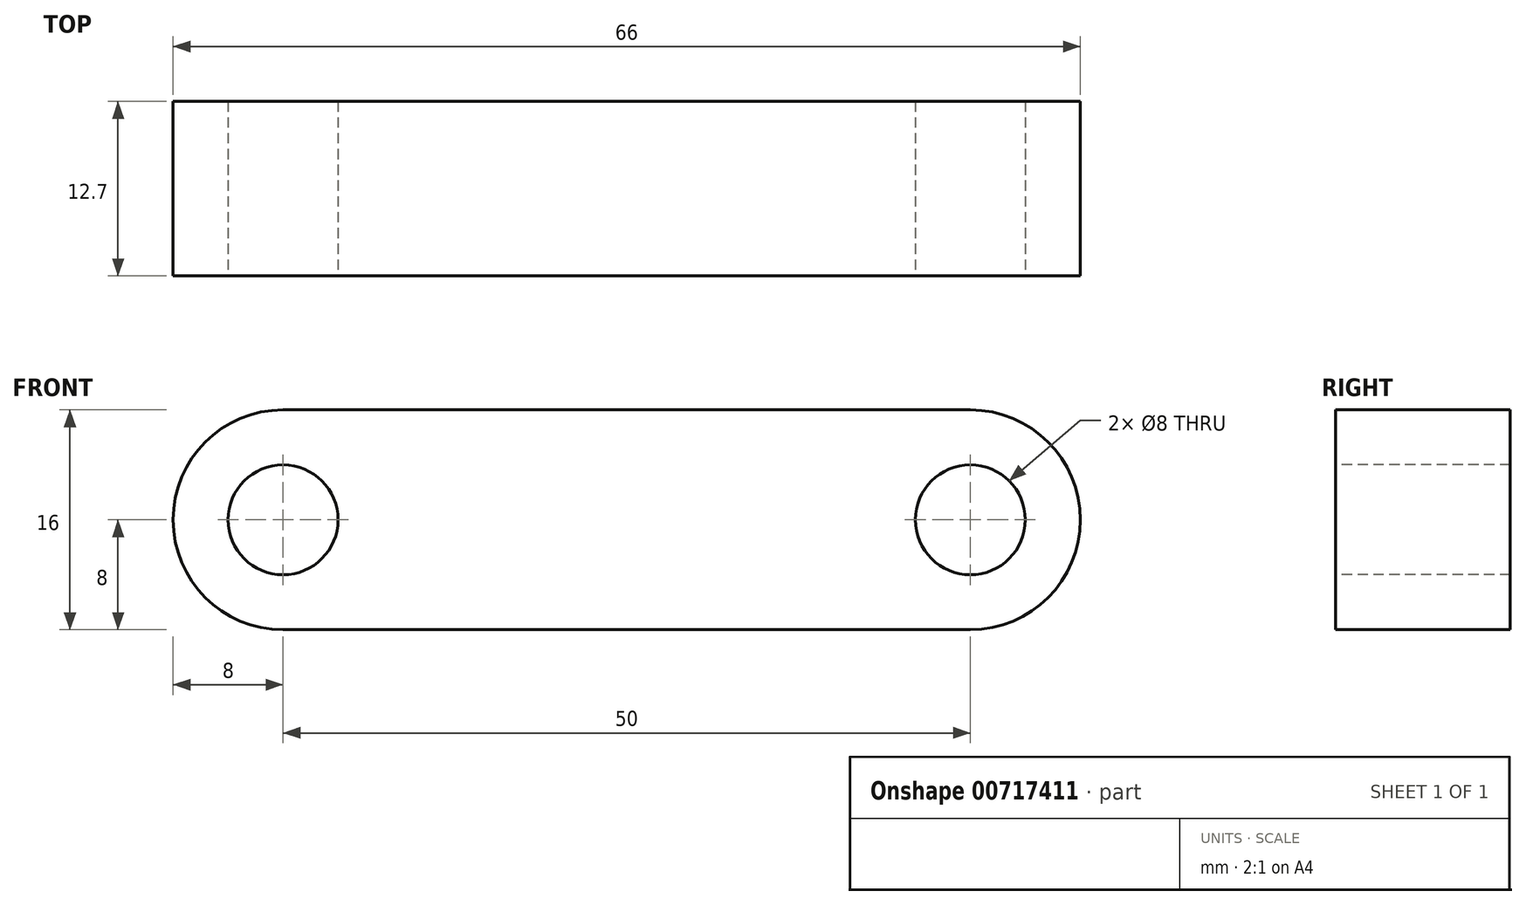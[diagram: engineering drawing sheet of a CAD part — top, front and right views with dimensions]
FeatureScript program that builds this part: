
annotation { "Feature Type Name" : "Feature", "Feature Type Description" : "" }
export const myFeature = defineFeature(function(context is Context, id is Id, definition is map)
    precondition{}
    {
        {
            var Q0;
            Q0=qCreatedBy(makeId("Front.planeOp"),FACE);
            var sketch = newSketch(context, id + "F0", { "sketchPlane" : qUnion([Q0])});
            skCircle(sketch, "E0", {"center": v(0, 0) * mm, "radius": 8 * mm});
            skCircle(sketch, "E1", {"center": v(-50, 0) * mm, "radius": 8 * mm});
            skLineSegment(sketch, "E2", {"start": v(-50, 8) * mm, "end": v(0, 8) * mm});
            skLineSegment(sketch, "E3", {"start": v(0, -8) * mm, "end": v(-50, -8) * mm});
            skSolve(sketch);
        }
        {
            var Q0;
            {var subQ0=sQuery(id+"F0.wireOp",EDGE,"E2");Q0=makeQuery(id+"F0.imprint","IMPRINT",FACE,{"disambiguationData":[TD([[makeQuery(id+"F0.imprint","IMPRINT",EDGE,{"derivedFrom":subQ0}),-1.0]])]});}
            var Q1;
            {var subQ0=sQuery(id+"F0.wireOp",EDGE,"E1");var subQ1=makeQuery(id+"F0.imprint","INTERSECT",VERTEX,{"derivedFrom":[subQ0,sQuery(id+"F0.wireOp",EDGE,"E2")]});Q1=makeQuery(id+"F0.imprint","IMPRINT",FACE,{"disambiguationData":[TD([[makeQuery(id+"F0.imprint","IMPRINT",EDGE,{"disambiguationData":[TD([[subQ1,-1.0]])],"derivedFrom":subQ0}),1.0]])]});}
            var Q2;
            {var subQ0=sQuery(id+"F0.wireOp",EDGE,"E0");var subQ1=makeQuery(id+"F0.imprint","INTERSECT",VERTEX,{"derivedFrom":[subQ0,sQuery(id+"F0.wireOp",EDGE,"E2")]});Q2=makeQuery(id+"F0.imprint","IMPRINT",FACE,{"disambiguationData":[TD([[makeQuery(id+"F0.imprint","IMPRINT",EDGE,{"disambiguationData":[TD([[subQ1,-1.0]])],"derivedFrom":subQ0}),1.0]])]});}
            extrude(context, id + "F1", {"entities" : qUnion([Q0, Q1, Q2]), "depth" : 12.7 * mm, "offsetDistance" : 25.4 * mm});
        }
        {
            var Q0;
            Q0=makeQuery(id+"F1.opExtrude","CAP_FACE",FACE,{"disambiguationData":[OSD([sQuery(id+"F0.wireOp",EDGE,"E0"),sQuery(id+"F0.wireOp",EDGE,"E1"),sQuery(id+"F0.wireOp",EDGE,"E2"),sQuery(id+"F0.wireOp",EDGE,"E3")])],"isStart":false});
            var sketch = newSketch(context, id + "F2", { "sketchPlane" : qUnion([Q0])});
            skCircle(sketch, "E4", {"center": v(-50, 0) * mm, "radius": 4 * mm});
            skCircle(sketch, "E5", {"center": v(0, 0) * mm, "radius": 4 * mm});
            skSolve(sketch);
        }
        {
            var Q0;
            Q0=makeQuery(id+"F2.imprint","IMPRINT",FACE,{"disambiguationData":[TD([[makeQuery(id+"F2.imprint","IMPRINT",EDGE,{"derivedFrom":sQuery(id+"F2.wireOp",EDGE,"E4")}),1.0]])]});
            var Q1;
            Q1=makeQuery(id+"F2.imprint","IMPRINT",FACE,{"disambiguationData":[TD([[makeQuery(id+"F2.imprint","IMPRINT",EDGE,{"derivedFrom":sQuery(id+"F2.wireOp",EDGE,"E5")}),1.0]])]});
            extrude(context, id + "F3", {"entities" : qUnion([Q0, Q1]), "operationType" : NewBodyOperationType.REMOVE, "endBound" : BoundingType.UP_TO_NEXT, "oppositeDirection" : true, "depth" : 25.4 * mm, "offsetDistance" : 25.4 * mm});
        }
    });
